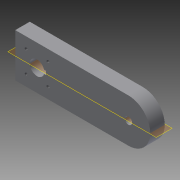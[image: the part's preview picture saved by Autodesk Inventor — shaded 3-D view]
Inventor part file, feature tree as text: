
AUTODESK INVENTOR PART (.ipt)
format: ipt  version: 2015 SP1 (Build 190203100, 203)  size: 105,984 bytes
history: native  units: in
note: dims shown in document units (in); Inventor stores cm internally (conversion verified against a paired STEP export)
features: sketch x2, extrude x1, plane x1, hole x1
ambient origin geometry x8: Origin, YZ Plane, XZ Plane, XY Plane, X Axis, Y Axis, Z Axis, Center Point
bodies: Body1 (feature_tree)
feature tree (5):
  extrude  "Extrusion2"  Depth=1.0in
  plane  "Work Plane1"
  hole  "Hole1"  [1 undecoded]
  sketch  "Sketch1"  dims[d0=3.0in d4=1.0in]
  sketch  "Sketch2"  dims[d13=0.5in d14=0.25in d15=6.3in d16=0.13in d17=1.5in d18=1.0in d19=0.0in d20=1.5in d21=1.5in d22=0.75in d23=0.75in d24=0.196in d25=0.75in d26=0.375in d27=0.25in d28=0.5635in d29=1.0in d30=0.8108in]
note: 1 required parameter value undecoded (feature->parameter linkage not recoverable at this tier; creation-order binding heuristic only, values carry confidence <= 0.55)
